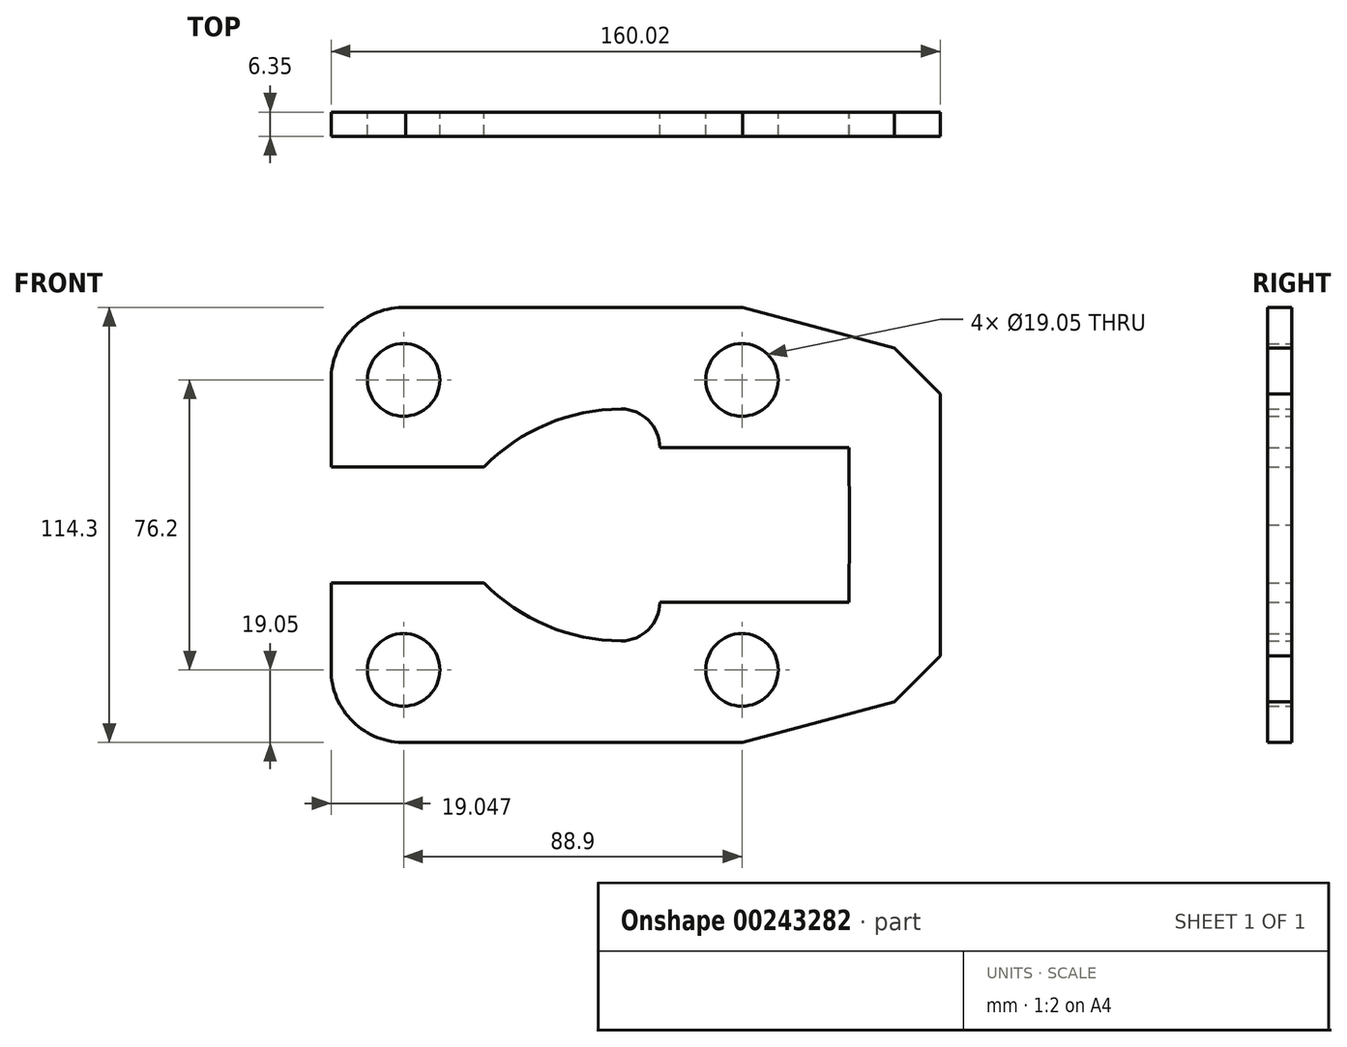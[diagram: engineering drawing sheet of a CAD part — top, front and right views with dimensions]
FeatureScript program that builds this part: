
annotation { "Feature Type Name" : "Feature", "Feature Type Description" : "" }
export const myFeature = defineFeature(function(context is Context, id is Id, definition is map)
    precondition{}
    {
        {
            var Q0;
            Q0=qCreatedBy(makeId("Front.planeOp"),FACE);
            var sketch = newSketch(context, id + "F0", { "sketchPlane" : qUnion([Q0])});
            skCircle(sketch, "E0", {"center": v(45.23, 38.1) * mm, "radius": 9.53 * mm});
            skLineSegment(sketch, "E1", {"start": v(-62.72, 38.1) * mm, "end": v(-62.72, 15.24) * mm});
            skArc(sketch, "E2", {"start": v(-43.14, 57.14) * mm, "mid": v(-56.96, 51.76) * mm, "end": v(-62.72, 38.1) * mm});
            skLineSegment(sketch, "E3", {"start": v(-44.2, 57.14) * mm, "end": v(45.4, 57.14) * mm});
            skLineSegment(sketch, "E4", {"start": v(97.3, 0) * mm, "end": v(97.3, 34.43) * mm});
            skLineSegment(sketch, "E5.MirrorCS", {"start": v(-62.72, -38.1) * mm, "end": v(-62.72, -15.24) * mm});
            skArc(sketch, "E6.MirrorCS", {"start": v(-43.14, -57.14) * mm, "mid": v(-56.96, -51.76) * mm, "end": v(-62.72, -38.1) * mm});
            skLineSegment(sketch, "E7.MirrorCS", {"start": v(-44.2, -57.14) * mm, "end": v(45.4, -57.14) * mm});
            skCircle(sketch, "E8.MirrorC", {"center": v(45.23, -38.1) * mm, "radius": 9.53 * mm});
            skLineSegment(sketch, "E9.MirrorCS", {"start": v(97.3, 0) * mm, "end": v(97.3, -34.43) * mm});
            skLineSegment(sketch, "E10", {"start": v(45.4, 57.14) * mm, "end": v(85.27, 46.46) * mm});
            skLineSegment(sketch, "E11", {"start": v(85.27, 46.46) * mm, "end": v(97.3, 34.43) * mm});
            skLineSegment(sketch, "E12.MirrorCS", {"start": v(45.4, -57.14) * mm, "end": v(85.27, -46.46) * mm});
            skLineSegment(sketch, "E13.MirrorCS", {"start": v(85.27, -46.46) * mm, "end": v(97.3, -34.43) * mm});
            skPoint(sketch, "E14.end.orphan", {"position": v(73.42, 0) * mm});
            skLineSegment(sketch, "E15", {"start": v(73.42, 0) * mm, "end": v(73.32, 20.32) * mm});
            skPoint(sketch, "E16.orphan", {"position": v(73.32, -20.32) * mm});
            skLineSegment(sketch, "E17", {"start": v(73.42, 0) * mm, "end": v(73.32, -20.32) * mm});
            skArc(sketch, "E18", {"start": v(23.64, 20.32) * mm, "mid": v(20.66, 27.5) * mm, "end": v(13.48, 30.48) * mm});
            skLineSegment(sketch, "E19", {"start": v(-62.72, 15.24) * mm, "end": v(-22.56, 15.24) * mm});
            skArc(sketch, "E20.MirrorC", {"start": v(23.64, -20.32) * mm, "mid": v(20.66, -27.5) * mm, "end": v(13.48, -30.48) * mm});
            skLineSegment(sketch, "E21.MirrorCS", {"start": v(73.32, -20.32) * mm, "end": v(23.64, -20.32) * mm});
            skLineSegment(sketch, "E22.MirrorCS", {"start": v(-62.72, -15.24) * mm, "end": v(-22.56, -15.24) * mm});
            skArc(sketch, "E23.MirrorC", {"start": v(13.48, -30.48) * mm, "mid": v(-6.07, -26.47) * mm, "end": v(-22.56, -15.24) * mm});
            skCircle(sketch, "E24", {"center": v(-43.67, 38.1) * mm, "radius": 9.53 * mm});
            skPoint(sketch, "E25.orphan", {"position": v(4.68, 15.24) * mm});
            skArc(sketch, "E26.trimOffspring", {"start": v(13.48, 30.48) * mm, "mid": v(-6.07, 26.47) * mm, "end": v(-22.56, 15.24) * mm});
            skPoint(sketch, "E27.orphan", {"position": v(4.68, -15.24) * mm});
            skLineSegment(sketch, "E28.MirrorCS", {"start": v(73.32, 20.32) * mm, "end": v(23.64, 20.32) * mm});
            skCircle(sketch, "E29.MirrorC", {"center": v(-43.67, -38.1) * mm, "radius": 9.53 * mm});
            skSolve(sketch);
        }
        {
            var Q0;
            Q0 = qSketchRegion(id + "F0", true);
            extrude(context, id + "F1", {"entities" : qUnion([Q0]), "depth" : 6.35 * mm});
        }
    });
